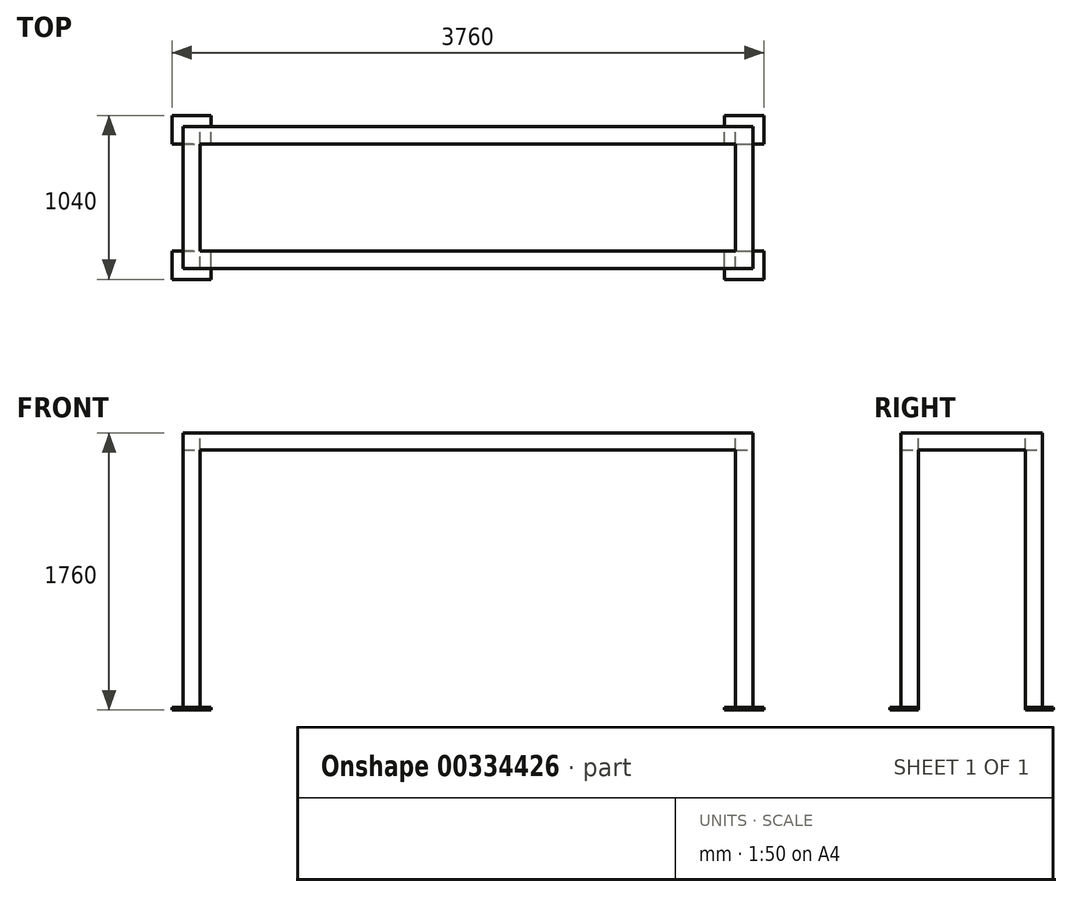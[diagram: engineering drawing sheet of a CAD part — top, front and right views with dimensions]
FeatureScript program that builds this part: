
annotation { "Feature Type Name" : "Feature", "Feature Type Description" : "" }
export const myFeature = defineFeature(function(context is Context, id is Id, definition is map)
    precondition{}
    {
        {
            var Q0;
            Q0=qCreatedBy(makeId("Front.planeOp"),FACE);
            var sketch = newSketch(context, id + "F0", { "sketchPlane" : qUnion([Q0])});
            skLineSegment(sketch, "E0.bottom", {"start": v(0, 0) * mm, "end": v(110, 0) * mm});
            skLineSegment(sketch, "E0.top", {"start": v(0, 1760) * mm, "end": v(3620, 1760) * mm});
            skLineSegment(sketch, "E0.left", {"start": v(0, 0) * mm, "end": v(0, 1760) * mm});
            skLineSegment(sketch, "E0.right", {"start": v(3620, 0) * mm, "end": v(3620, 1760) * mm});
            skLineSegment(sketch, "E1.0", {"start": v(110, 1650) * mm, "end": v(3510, 1650) * mm});
            skLineSegment(sketch, "E2.0", {"start": v(110, 0) * mm, "end": v(110, 1650) * mm});
            skLineSegment(sketch, "E3.0", {"start": v(3510, 0) * mm, "end": v(3510, 1650) * mm});
            skLineSegment(sketch, "E4.trimOffspring", {"start": v(3510, 0) * mm, "end": v(3620, 0) * mm});
            skLineSegment(sketch, "E5.bottom", {"start": v(180, 15) * mm, "end": v(-70, 15) * mm});
            skLineSegment(sketch, "E5.left", {"start": v(180, 15) * mm, "end": v(180, 0) * mm});
            skLineSegment(sketch, "E5.right", {"start": v(-70, 15) * mm, "end": v(-70, 0) * mm});
            skPoint(sketch, "E5.middle", {"position": v(55, 0) * mm});
            skLineSegment(sketch, "E6", {"start": v(-70, 0) * mm, "end": v(180, 0) * mm});
            skLineSegment(sketch, "E7", {"start": v(1810, 1650) * mm, "end": v(1810, 902.8) * mm, "construction": true});
            skLineSegment(sketch, "E8.MirrorCS", {"start": v(3690, 15) * mm, "end": v(3690, 0) * mm});
            skLineSegment(sketch, "E9.MirrorCS", {"start": v(3440, 15) * mm, "end": v(3440, 0) * mm});
            skLineSegment(sketch, "E10.MirrorCS", {"start": v(3620, 0) * mm, "end": v(3510, 0) * mm});
            skPoint(sketch, "E11.MirrorP", {"position": v(3565, 0) * mm});
            skLineSegment(sketch, "E12.MirrorCS", {"start": v(3440, 15) * mm, "end": v(3690, 15) * mm});
            skLineSegment(sketch, "E13.MirrorCS", {"start": v(3690, 0) * mm, "end": v(3440, 0) * mm});
            skSolve(sketch);
        }
        {
            var Q0;
            {var subQ1=sQuery(id+"F0.wireOp",EDGE,"E0.top");Q0=makeQuery(id+"F0.imprint","IMPRINT",FACE,{"disambiguationData":[TD([[makeQuery(id+"F0.imprint","IMPRINT",EDGE,{"derivedFrom":subQ1}),-1.0]])]});}
            extrude(context, id + "F1", {"entities" : qUnion([Q0]), "depth" : 900 * mm});
        }
        {
            var Q0;
            {var subQ5=sQuery(id+"F0.wireOp",EDGE,"E5.left");Q0=makeQuery(id+"F0.imprint","IMPRINT",FACE,{"disambiguationData":[TD([[makeQuery(id+"F0.imprint","IMPRINT",EDGE,{"derivedFrom":subQ5}),-1.0]])]});}
            var Q1;
            {var subQ5=sQuery(id+"F0.wireOp",EDGE,"E5.right");Q1=makeQuery(id+"F0.imprint","IMPRINT",FACE,{"disambiguationData":[TD([[makeQuery(id+"F0.imprint","IMPRINT",EDGE,{"derivedFrom":subQ5}),1.0]])]});}
            var Q2;
            {var subQ0=sQuery(id+"F0.wireOp",EDGE,"E6");var subQ1=sQuery(id+"F0.wireOp",EDGE,"E0.left");var subQ2=makeQuery(id+"F0.imprint","INTERSECT",VERTEX,{"derivedFrom":[subQ1,subQ0]});Q2=makeQuery(id+"F0.imprint","IMPRINT",FACE,{"disambiguationData":[TD([[makeQuery(id+"F0.imprint","IMPRINT",EDGE,{"disambiguationData":[TD([[subQ2,-1.0]])],"derivedFrom":subQ1}),-1.0]])]});}
            var Q3;
            {var subQ5=sQuery(id+"F0.wireOp",EDGE,"E9.MirrorCS");Q3=makeQuery(id+"F0.imprint","IMPRINT",FACE,{"disambiguationData":[TD([[makeQuery(id+"F0.imprint","IMPRINT",EDGE,{"derivedFrom":subQ5}),1.0]])]});}
            var Q4;
            {var subQ0=sQuery(id+"F0.wireOp",EDGE,"E13.MirrorCS");var subQ1=sQuery(id+"F0.wireOp",EDGE,"E0.right");var subQ2=makeQuery(id+"F0.imprint","INTERSECT",VERTEX,{"derivedFrom":[subQ1,subQ0]});Q4=makeQuery(id+"F0.imprint","IMPRINT",FACE,{"disambiguationData":[TD([[makeQuery(id+"F0.imprint","IMPRINT",EDGE,{"disambiguationData":[TD([[subQ2,-1.0]])],"derivedFrom":subQ1}),1.0]])]});}
            var Q5;
            {var subQ5=sQuery(id+"F0.wireOp",EDGE,"E8.MirrorCS");Q5=makeQuery(id+"F0.imprint","IMPRINT",FACE,{"disambiguationData":[TD([[makeQuery(id+"F0.imprint","IMPRINT",EDGE,{"derivedFrom":subQ5}),-1.0]])]});}
            extrude(context, id + "F2", {"entities" : qUnion([Q0, Q1, Q2, Q3, Q4, Q5]), "operationType" : NewBodyOperationType.ADD, "depth" : (900 + 125 - 55) * mm, "hasSecondDirection" : true, "secondDirectionOppositeDirection" : true, "secondDirectionDepth" : (125 - 110 / 2) * mm});
        }
        {
            var Q0;
            Q0=makeQuery(id+"F1.opExtrude","SWEPT_FACE",FACE,{"disambiguationData":[OSD([sQuery(id+"F0.wireOp",EDGE,"E0.right")])]});
            var sketch = newSketch(context, id + "F3", { "sketchPlane" : qUnion([Q0])});
            skLineSegment(sketch, "E14.0", {"start": v(-900, 1760) * mm, "end": v(0, 1760) * mm});
            skLineSegment(sketch, "E14.1", {"start": v(-900, 15) * mm, "end": v(-900, 1760) * mm});
            skLineSegment(sketch, "E15.0", {"start": v(0, 15) * mm, "end": v(0, 1760) * mm});
            skLineSegment(sketch, "E16.0", {"start": v(-110, -251.93) * mm, "end": v(-110, 1650) * mm});
            skLineSegment(sketch, "E16.1", {"start": v(-790, 1650) * mm, "end": v(-110, 1650) * mm});
            skLineSegment(sketch, "E16.2", {"start": v(-790, -251.93) * mm, "end": v(-790, 1650) * mm});
            skLineSegment(sketch, "E17", {"start": v(-110, -251.93) * mm, "end": v(-790, -251.93) * mm});
            skSolve(sketch);
        }
        {
            var Q0;
            Q0 = qSketchRegion(id + "F3", true);
            extrude(context, id + "F4", {"entities" : qUnion([Q0]), "operationType" : NewBodyOperationType.REMOVE, "endBound" : BoundingType.SYMMETRIC, "oppositeDirection" : true, "depth" : 9000 * mm});
        }
        {
            var Q0;
            Q0=makeQuery(id+"F1.opExtrude","SWEPT_FACE",FACE,{"disambiguationData":[OSD([sQuery(id+"F0.wireOp",EDGE,"E0.top")])]});
            var sketch = newSketch(context, id + "F5", { "sketchPlane" : qUnion([Q0])});
            skLineSegment(sketch, "E18.0", {"start": v(110, -790) * mm, "end": v(3510, -790) * mm});
            skLineSegment(sketch, "E18.1", {"start": v(110, -790) * mm, "end": v(110, -110) * mm});
            skLineSegment(sketch, "E18.2", {"start": v(110, -110) * mm, "end": v(3510, -110) * mm});
            skLineSegment(sketch, "E18.3", {"start": v(3510, -790) * mm, "end": v(3510, -110) * mm});
            skSolve(sketch);
        }
        {
            var Q0;
            Q0=makeQuery(id+"F5.imprint","IMPRINT",FACE,{"disambiguationData":[TD([[makeQuery(id+"F5.imprint","IMPRINT",EDGE,{"derivedFrom":sQuery(id+"F5.wireOp",EDGE,"E18.0")}),1.0]])]});
            extrude(context, id + "F6", {"entities" : qUnion([Q0]), "operationType" : NewBodyOperationType.REMOVE, "oppositeDirection" : true, "depth" : 120 * mm});
        }
        {
            var Q0;
            {var subQ0=sQuery(id+"F0.wireOp",EDGE,"E6");Q0=makeQuery(id+"F4.boolean.opBoolean","SPLIT",FACE,{"disambiguationData":[TD([makeQuery(id+"F4.opExtrude","SWEPT_FACE",FACE,{"disambiguationData":[OSD([sQuery(id+"F3.wireOp",EDGE,"E16.0")])]})])],"derivedFrom":makeQuery(id+"F2.opExtrude","SWEPT_FACE",FACE,{"disambiguationData":[OSD([subQ0])]})});}
            cPlane(context, id + "F7", {"entities" : qUnion([Q0]), "cplaneType" : CPlaneType.OFFSET, "offset" : 0 * mm, "width" : 150 * mm, "height" : 150 * mm});
        }
        {
            var Q0;
            Q0=qCreatedBy(id+"F7.planeOp",FACE);
            var sketch = newSketch(context, id + "F8", { "sketchPlane" : qUnion([Q0])});
            skLineSegment(sketch, "E19", {"start": v(1810, 900) * mm, "end": v(1810, 0) * mm, "construction": true});
            skLineSegment(sketch, "E20", {"start": v(0, 450) * mm, "end": v(3620, 450) * mm, "construction": true});
            skSolve(sketch);
        }
    });
